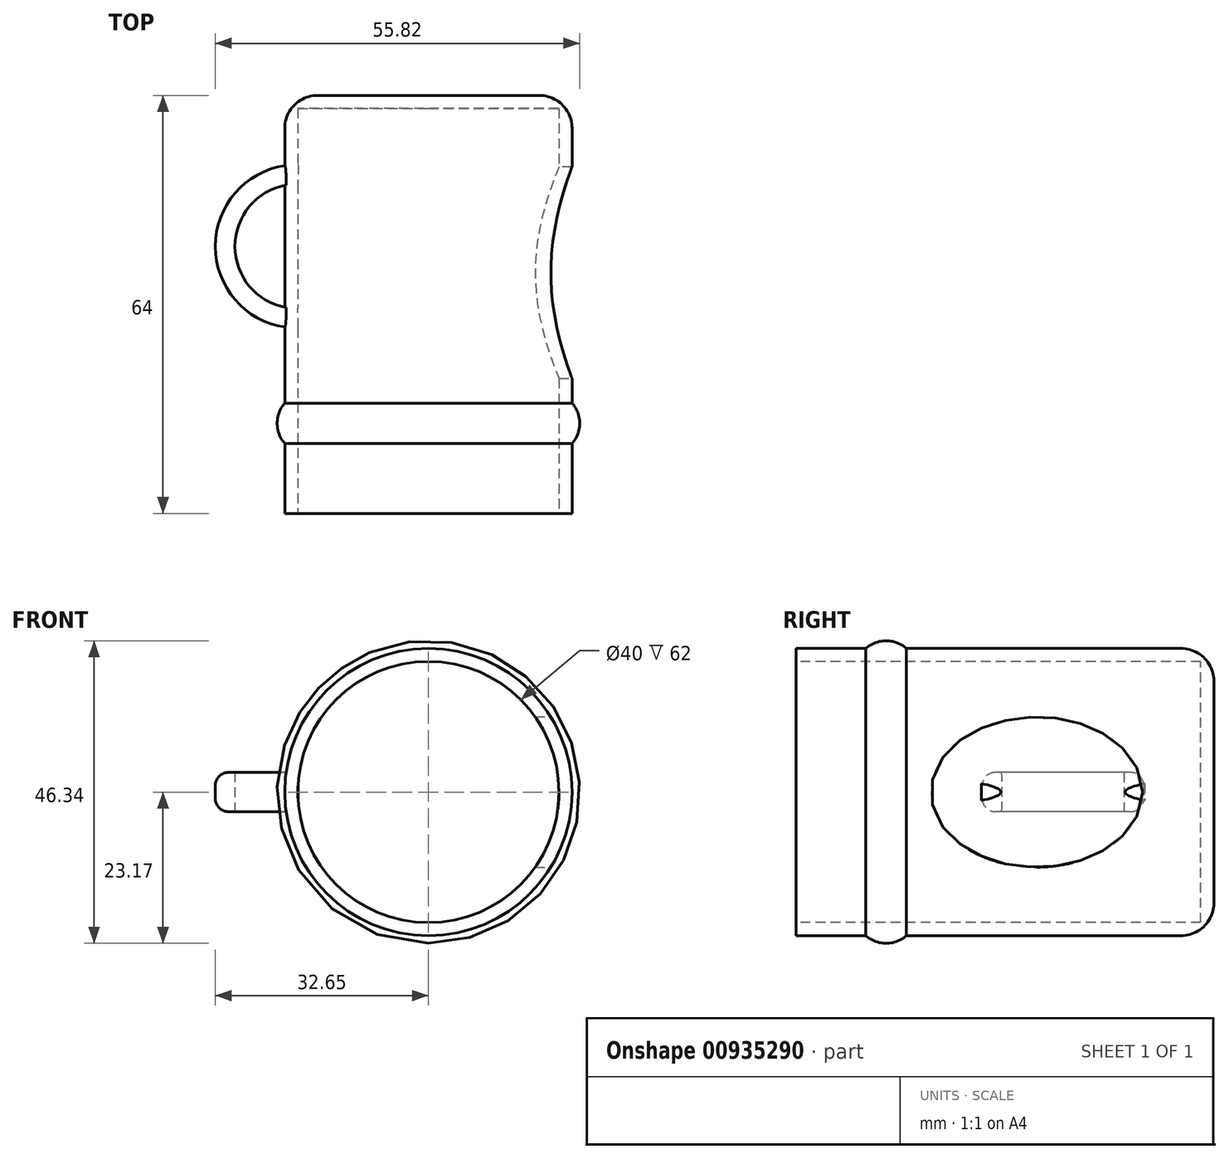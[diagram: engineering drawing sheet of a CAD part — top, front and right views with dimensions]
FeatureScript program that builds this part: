
annotation { "Feature Type Name" : "Feature", "Feature Type Description" : "" }
export const myFeature = defineFeature(function(context is Context, id is Id, definition is map)
    precondition{}
    {
        {
            var Q0;
            Q0=qCreatedBy(makeId("Top.planeOp"),FACE);
            var sketch = newSketch(context, id + "F0", { "sketchPlane" : qUnion([Q0])});
            skLineSegment(sketch, "E0", {"start": v(0, 43.26) * mm, "end": v(-20, 43.26) * mm});
            skLineSegment(sketch, "E1", {"start": v(-20, 43.26) * mm, "end": v(-20, -18.74) * mm});
            skLineSegment(sketch, "E2.0", {"start": v(-22, 45.26) * mm, "end": v(-22, -18.74) * mm});
            skLineSegment(sketch, "E2.1", {"start": v(0, 45.26) * mm, "end": v(-22, 45.26) * mm});
            skLineSegment(sketch, "E3", {"start": v(-22, -18.74) * mm, "end": v(-20, -18.74) * mm});
            skLineSegment(sketch, "E4", {"start": v(0, 45.26) * mm, "end": v(0, 43.26) * mm});
            skLineSegment(sketch, "E5", {"start": v(0, -17.3) * mm, "end": v(0, 13.08) * mm, "construction": true});
            skArc(sketch, "E6", {"start": v(-22, -1.85) * mm, "mid": v(-23.17, -4.94) * mm, "end": v(-22, -8.04) * mm});
            skSolve(sketch);
        }
        {
            var Q0;
            Q0 = qSketchRegion(id + "F0", true);
            var Q1;
            Q1=sQuery(id+"F0.wireOp",EDGE,"E5");
            revolve(context, id + "F1", {"surfaceOperationType" : NewSurfaceOperationType.NEW, "entities" : qUnion([Q0]), "axis" : qUnion([Q1]), "revolveType" : RevolveType.FULL});
        }
        {
            var Q0;
            Q0=qCreatedBy(makeId("Top.planeOp"),FACE);
            var sketch = newSketch(context, id + "F2", { "sketchPlane" : qUnion([Q0])});
            skArc(sketch, "E7", {"start": v(-20, 31.66) * mm, "mid": v(-29.65, 22.15) * mm, "end": v(-20, 12.64) * mm});
            skArc(sketch, "E8.0", {"start": v(-19.96, 34.66) * mm, "mid": v(-32.65, 22.15) * mm, "end": v(-19.96, 9.64) * mm});
            skLineSegment(sketch, "E9", {"start": v(-19.96, 34.66) * mm, "end": v(-20, 31.66) * mm});
            skLineSegment(sketch, "E10", {"start": v(-20, 12.64) * mm, "end": v(-19.96, 9.64) * mm});
            skLineSegment(sketch, "E11", {"start": v(-23, 39.77) * mm, "end": v(-23, 37.34) * mm, "construction": true});
            skSolve(sketch);
        }
        {
            var Q0;
            Q0=makeQuery(id+"F2.imprint","IMPRINT",FACE,{"disambiguationData":[TD([[makeQuery(id+"F2.imprint","IMPRINT",EDGE,{"derivedFrom":sQuery(id+"F2.wireOp",EDGE,"E7")}),-1.0]])]});
            extrude(context, id + "F3", {"entities" : qUnion([Q0]), "operationType" : NewBodyOperationType.ADD, "endBound" : BoundingType.SYMMETRIC, "depth" : 6 * mm, "offsetDistance" : 25 * mm});
        }
        {
            var Q0;
            Q0=makeQuery(id+"F1.opRevolve","SWEPT_EDGE",EDGE,{"disambiguationData":[OSD([sQuery(id+"F0.wireOp",EDGE,"E2.0"),sQuery(id+"F0.wireOp",EDGE,"E2.1")])]});
            fillet(context, id + "F4", {"entities" : qUnion([Q0]), "radius" : 5 * mm, "tangentPropagation" : true, "allowEdgeOverflow" : false});
        }
        {
            var Q0;
            Q0=makeQuery(id+"F3.opExtrude","CAP_EDGE",EDGE,{"disambiguationData":[OSD([sQuery(id+"F2.wireOp",EDGE,"E8.0")])],"isStart":false});
            var Q1;
            Q1=makeQuery(id+"F3.opExtrude","CAP_EDGE",EDGE,{"disambiguationData":[OSD([sQuery(id+"F2.wireOp",EDGE,"E8.0")])],"isStart":true});
            fillet(context, id + "F5", {"entities" : qUnion([Q0, Q1]), "radius" : 2 * mm, "tangentPropagation" : true, "allowEdgeOverflow" : false});
        }
        {
            var Q0;
            Q0=qCreatedBy(makeId("Right.planeOp"),FACE);
            var sketch = newSketch(context, id + "F6", { "sketchPlane" : qUnion([Q0])});
            skEllipse(sketch, "E12", {"center": v(18.12, 0) * mm, "majorRadius": 16.21 * mm, "minorRadius": 11.5 * mm, "majorAxis": v(1, 0)});
            skSolve(sketch);
        }
        {
            var Q0;
            Q0=makeQuery(id+"F6.imprint","IMPRINT",FACE,{"disambiguationData":[TD([[makeQuery(id+"F6.imprint","IMPRINT",EDGE,{"derivedFrom":sQuery(id+"F6.wireOp",EDGE,"E12")}),1.0]])]});
            extrude(context, id + "F7", {"entities" : qUnion([Q0]), "operationType" : NewBodyOperationType.REMOVE, "depth" : 30 * mm, "offsetDistance" : 25 * mm});
        }
    });
